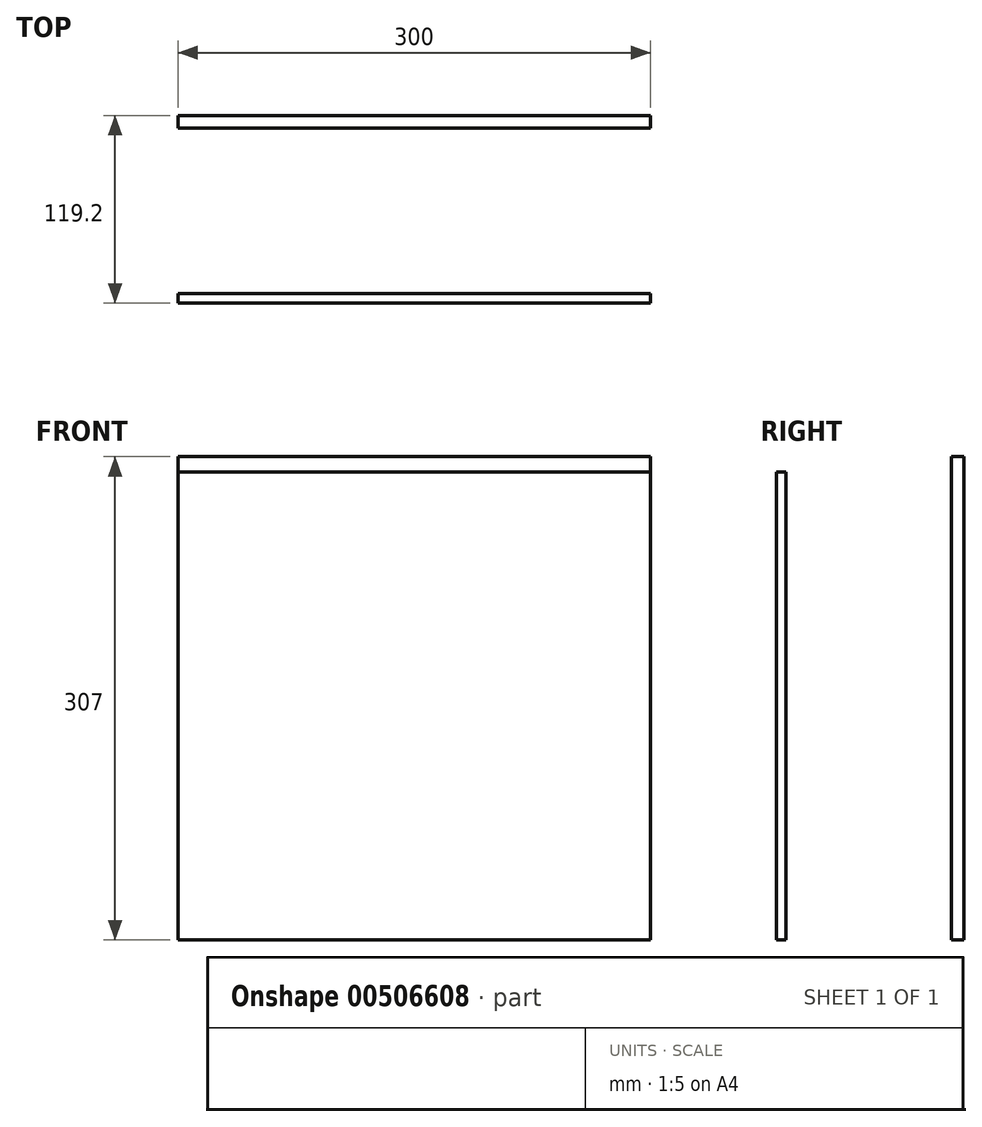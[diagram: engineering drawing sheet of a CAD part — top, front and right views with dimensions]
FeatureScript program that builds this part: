
annotation { "Feature Type Name" : "Feature", "Feature Type Description" : "" }
export const myFeature = defineFeature(function(context is Context, id is Id, definition is map)
    precondition{}
    {
        {
            var Q0;
            Q0=qCreatedBy(makeId("Right.planeOp"),FACE);
            var sketch = newSketch(context, id + "F0", { "sketchPlane" : qUnion([Q0])});
            skLineSegment(sketch, "E0.bottom", {"start": v(105.2, 9.76) * mm, "end": v(113.2, 9.76) * mm});
            skLineSegment(sketch, "E0.top", {"start": v(105.2, -297.24) * mm, "end": v(113.2, -297.24) * mm});
            skLineSegment(sketch, "E0.left", {"start": v(105.2, 9.76) * mm, "end": v(105.2, -297.24) * mm});
            skLineSegment(sketch, "E0.right", {"start": v(113.2, 9.76) * mm, "end": v(113.2, -297.24) * mm});
            skLineSegment(sketch, "E1.bottom", {"start": v(-6, 0) * mm, "end": v(0, 0) * mm});
            skLineSegment(sketch, "E1.top", {"start": v(-6, -297.24) * mm, "end": v(0, -297.24) * mm});
            skLineSegment(sketch, "E1.left", {"start": v(-6, 0) * mm, "end": v(-6, -297.24) * mm});
            skLineSegment(sketch, "E1.right", {"start": v(0, 0) * mm, "end": v(0, -297.24) * mm});
            skLineSegment(sketch, "E2", {"start": v(113.2, -297.24) * mm, "end": v(-197.1, -297.24) * mm, "construction": true});
            skSolve(sketch);
        }
        {
            var Q0;
            Q0=makeQuery(id+"F0.imprint","IMPRINT",FACE,{"disambiguationData":[TD([[makeQuery(id+"F0.imprint","IMPRINT",EDGE,{"derivedFrom":sQuery(id+"F0.wireOp",EDGE,"E0.bottom")}),-1.0]])]});
            var Q1;
            Q1=makeQuery(id+"F0.imprint","IMPRINT",FACE,{"disambiguationData":[TD([[makeQuery(id+"F0.imprint","IMPRINT",EDGE,{"derivedFrom":sQuery(id+"F0.wireOp",EDGE,"E1.bottom")}),-1.0]])]});
            extrude(context, id + "F1", {"entities" : qUnion([Q0, Q1]), "oppositeDirection" : true, "depth" : 300 * mm});
        }
        {
            var Q0;
            Q0=qCreatedBy(makeId("Right.planeOp"),FACE);
            cPlane(context, id + "F2", {"entities" : qUnion([Q0]), "cplaneType" : CPlaneType.OFFSET, "offset" : 50 * mm, "oppositeDirection" : true, "width" : 150 * mm, "height" : 150 * mm});
        }
    });
